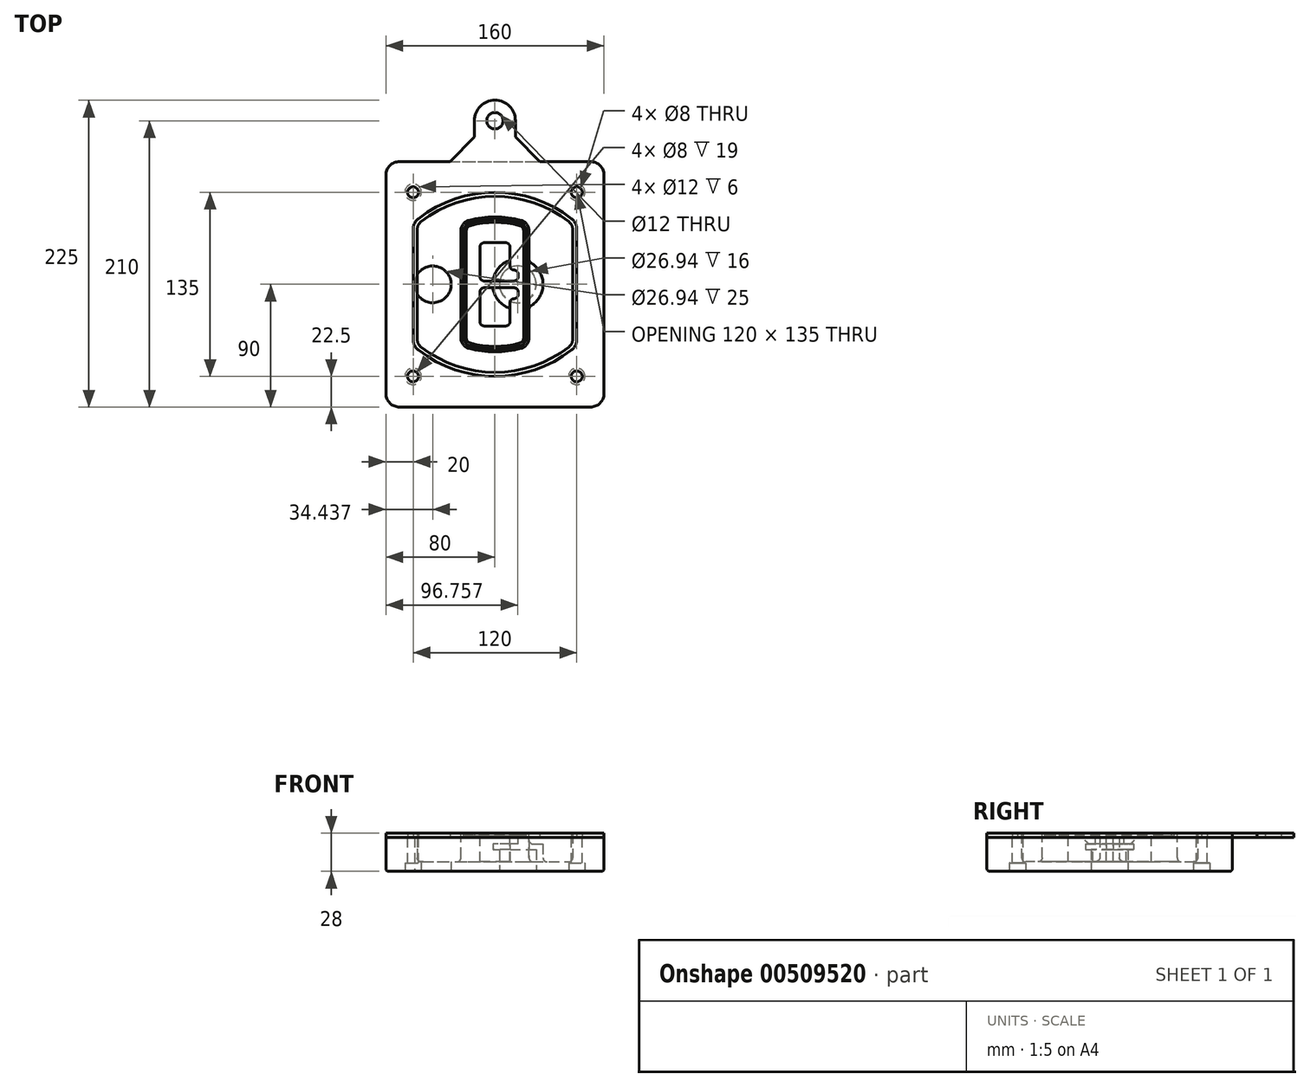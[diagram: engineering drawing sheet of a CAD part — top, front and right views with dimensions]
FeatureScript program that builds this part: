
annotation { "Feature Type Name" : "Feature", "Feature Type Description" : "" }
export const myFeature = defineFeature(function(context is Context, id is Id, definition is map)
    precondition{}
    {
        {
            var Q0;
            Q0=qCreatedBy(makeId("Top.planeOp"),FACE);
            var sketch = newSketch(context, id + "F0", { "sketchPlane" : qUnion([Q0])});
            skPoint(sketch, "E0.rect.middle", {"position": v(0, 0) * mm});
            skLineSegment(sketch, "E1.bottom", {"start": v(-70, -90) * mm, "end": v(70, -90) * mm});
            skLineSegment(sketch, "E1.top", {"start": v(-70, 90) * mm, "end": v(70, 90) * mm});
            skLineSegment(sketch, "E1.left", {"start": v(-80, -80) * mm, "end": v(-80, 80) * mm});
            skLineSegment(sketch, "E1.right", {"start": v(80, -80) * mm, "end": v(80, 80) * mm});
            skLineSegment(sketch, "E2", {"start": v(-80, 90) * mm, "end": v(80, -90) * mm, "construction": true});
            skLineSegment(sketch, "E3", {"start": v(80, 90) * mm, "end": v(-80, -90) * mm, "construction": true});
            skCircle(sketch, "E4", {"center": v(-60, 67.5) * mm, "radius": 4 * mm});
            skCircle(sketch, "E5", {"center": v(60, 67.5) * mm, "radius": 4 * mm});
            skCircle(sketch, "E6", {"center": v(60, -67.5) * mm, "radius": 4 * mm});
            skCircle(sketch, "E7", {"center": v(-60, -67.5) * mm, "radius": 4 * mm});
            skLineSegment(sketch, "E8", {"start": v(-60, 67.5) * mm, "end": v(60, 67.5) * mm, "construction": true});
            skLineSegment(sketch, "E9", {"start": v(60, 67.5) * mm, "end": v(60, -67.5) * mm, "construction": true});
            skLineSegment(sketch, "E10", {"start": v(60, -67.5) * mm, "end": v(-60, -67.5) * mm, "construction": true});
            skLineSegment(sketch, "E11", {"start": v(-60, -67.5) * mm, "end": v(-60, 67.5) * mm, "construction": true});
            skLineSegment(sketch, "E12", {"start": v(-60, 40.3) * mm, "end": v(-60, -40.3) * mm});
            skLineSegment(sketch, "E13", {"start": v(60, 40.3) * mm, "end": v(60, -40.3) * mm});
            skArc(sketch, "E14", {"start": v(56.15, 48.18) * mm, "mid": v(0, 67.5) * mm, "end": v(-56.15, 48.18) * mm});
            skArc(sketch, "E15", {"start": v(-56.15, -48.18) * mm, "mid": v(0, -67.5) * mm, "end": v(56.15, -48.18) * mm});
            skLineSegment(sketch, "E16", {"start": v(-60, 0) * mm, "end": v(60, 0) * mm, "construction": true});
            skPoint(sketch, "E17.visualSharp", {"position": v(-60, -45) * mm});
            skArc(sketch, "E17.filletArc", {"start": v(-60, -40.3) * mm, "mid": v(-58.99, -44.68) * mm, "end": v(-56.15, -48.18) * mm});
            skPoint(sketch, "E18.visualSharp", {"position": v(-60, 45) * mm});
            skArc(sketch, "E18.filletArc", {"start": v(-56.15, 48.18) * mm, "mid": v(-58.99, 44.68) * mm, "end": v(-60, 40.3) * mm});
            skPoint(sketch, "E19.visualSharp", {"position": v(60, 45) * mm});
            skArc(sketch, "E19.filletArc", {"start": v(60, 40.3) * mm, "mid": v(58.99, 44.68) * mm, "end": v(56.15, 48.18) * mm});
            skPoint(sketch, "E20.visualSharp", {"position": v(60, -45) * mm});
            skArc(sketch, "E20.filletArc", {"start": v(56.15, -48.18) * mm, "mid": v(58.99, -44.68) * mm, "end": v(60, -40.3) * mm});
            skPoint(sketch, "E21.visualSharp", {"position": v(-80, 90) * mm});
            skArc(sketch, "E21.filletArc", {"start": v(-70, 90) * mm, "mid": v(-77.07, 87.07) * mm, "end": v(-80, 80) * mm});
            skPoint(sketch, "E22.visualSharp", {"position": v(80, 90) * mm});
            skArc(sketch, "E22.filletArc", {"start": v(80, 80) * mm, "mid": v(77.07, 87.07) * mm, "end": v(70, 90) * mm});
            skPoint(sketch, "E23.visualSharp", {"position": v(80, -90) * mm});
            skArc(sketch, "E23.filletArc", {"start": v(70, -90) * mm, "mid": v(77.07, -87.07) * mm, "end": v(80, -80) * mm});
            skPoint(sketch, "E24.visualSharp", {"position": v(-80, -90) * mm});
            skArc(sketch, "E24.filletArc", {"start": v(-80, -80) * mm, "mid": v(-77.07, -87.07) * mm, "end": v(-70, -90) * mm});
            skArc(sketch, "E25.0", {"start": v(57, 40.3) * mm, "mid": v(56.3, 43.36) * mm, "end": v(54.3, 45.81) * mm});
            skLineSegment(sketch, "E25.1", {"start": v(57, 40.3) * mm, "end": v(57, -40.3) * mm});
            skArc(sketch, "E25.2", {"start": v(54.3, -45.81) * mm, "mid": v(56.3, -43.36) * mm, "end": v(57, -40.3) * mm});
            skArc(sketch, "E25.3", {"start": v(-54.3, -45.81) * mm, "mid": v(0, -64.5) * mm, "end": v(54.3, -45.81) * mm});
            skArc(sketch, "E25.4", {"start": v(-57, -40.3) * mm, "mid": v(-56.3, -43.36) * mm, "end": v(-54.3, -45.81) * mm});
            skArc(sketch, "E25.5", {"start": v(54.3, 45.81) * mm, "mid": v(0, 64.5) * mm, "end": v(-54.3, 45.81) * mm});
            skLineSegment(sketch, "E25.6", {"start": v(-57, 40.3) * mm, "end": v(-57, -40.3) * mm});
            skArc(sketch, "E25.7", {"start": v(-54.3, 45.81) * mm, "mid": v(-56.3, 43.36) * mm, "end": v(-57, 40.3) * mm});
            skArc(sketch, "E26.0", {"start": v(-58.62, 51.33) * mm, "mid": v(-62.58, 46.43) * mm, "end": v(-64, 40.3) * mm});
            skArc(sketch, "E26.1", {"start": v(58.62, 51.33) * mm, "mid": v(0, 71.5) * mm, "end": v(-58.62, 51.33) * mm});
            skArc(sketch, "E26.2", {"start": v(64, 40.3) * mm, "mid": v(62.58, 46.43) * mm, "end": v(58.62, 51.33) * mm});
            skLineSegment(sketch, "E26.3", {"start": v(64, 40.3) * mm, "end": v(64, -40.3) * mm});
            skArc(sketch, "E26.4", {"start": v(58.62, -51.33) * mm, "mid": v(62.58, -46.43) * mm, "end": v(64, -40.3) * mm});
            skLineSegment(sketch, "E26.5", {"start": v(-64, 40.3) * mm, "end": v(-64, -40.3) * mm});
            skArc(sketch, "E26.6", {"start": v(-58.62, -51.33) * mm, "mid": v(0, -71.5) * mm, "end": v(58.62, -51.33) * mm});
            skArc(sketch, "E26.7", {"start": v(-64, -40.3) * mm, "mid": v(-62.58, -46.43) * mm, "end": v(-58.62, -51.33) * mm});
            skSolve(sketch);
        }
        {
            var Q0;
            Q0=makeQuery(id+"F0.imprint","IMPRINT",FACE,{"disambiguationData":[TD([[makeQuery(id+"F0.imprint","IMPRINT",EDGE,{"derivedFrom":sQuery(id+"F0.wireOp",EDGE,"E1.bottom")}),1.0]])]});
            var Q1;
            Q1=makeQuery(id+"F0.imprint","IMPRINT",FACE,{"disambiguationData":[TD([[makeQuery(id+"F0.imprint","IMPRINT",EDGE,{"derivedFrom":sQuery(id+"F0.wireOp",EDGE,"E12")}),1.0]])]});
            var Q2;
            Q2=makeQuery(id+"F0.imprint","IMPRINT",FACE,{"disambiguationData":[TD([[makeQuery(id+"F0.imprint","IMPRINT",EDGE,{"derivedFrom":sQuery(id+"F0.wireOp",EDGE,"E25.0")}),1.0]])]});
            var Q3;
            Q3=makeQuery(id+"F0.imprint","IMPRINT",FACE,{"disambiguationData":[TD([[makeQuery(id+"F0.imprint","IMPRINT",EDGE,{"derivedFrom":sQuery(id+"F0.wireOp",EDGE,"E12")}),-1.0]])]});
            extrude(context, id + "F1", {"entities" : qUnion([Q0, Q1, Q2, Q3]), "oppositeDirection" : true, "depth" : 25 * mm});
        }
        {
            var Q0;
            Q0=makeQuery(id+"F0.imprint","IMPRINT",FACE,{"disambiguationData":[TD([[makeQuery(id+"F0.imprint","IMPRINT",EDGE,{"derivedFrom":sQuery(id+"F0.wireOp",EDGE,"E12")}),1.0]])]});
            extrude(context, id + "F2", {"entities" : qUnion([Q0]), "operationType" : NewBodyOperationType.ADD, "depth" : 3 * mm});
        }
        {
            var Q0;
            Q0=makeQuery(id+"F0.imprint","IMPRINT",FACE,{"disambiguationData":[TD([[makeQuery(id+"F0.imprint","IMPRINT",EDGE,{"derivedFrom":sQuery(id+"F0.wireOp",EDGE,"E25.0")}),1.0]])]});
            extrude(context, id + "F3", {"entities" : qUnion([Q0]), "operationType" : NewBodyOperationType.REMOVE, "oppositeDirection" : true, "depth" : 18 * mm});
        }
        {
            var Q0;
            Q0=makeQuery(id+"F2.opExtrude","CAP_FACE",FACE,{"disambiguationData":[OSD([sQuery(id+"F0.wireOp",EDGE,"E12"),sQuery(id+"F0.wireOp",EDGE,"E13"),sQuery(id+"F0.wireOp",EDGE,"E14"),sQuery(id+"F0.wireOp",EDGE,"E15"),sQuery(id+"F0.wireOp",EDGE,"E17.filletArc"),sQuery(id+"F0.wireOp",EDGE,"E18.filletArc"),sQuery(id+"F0.wireOp",EDGE,"E19.filletArc"),sQuery(id+"F0.wireOp",EDGE,"E20.filletArc"),sQuery(id+"F0.wireOp",EDGE,"E25.0"),sQuery(id+"F0.wireOp",EDGE,"E25.1"),sQuery(id+"F0.wireOp",EDGE,"E25.2"),sQuery(id+"F0.wireOp",EDGE,"E25.3"),sQuery(id+"F0.wireOp",EDGE,"E25.4"),sQuery(id+"F0.wireOp",EDGE,"E25.5"),sQuery(id+"F0.wireOp",EDGE,"E25.6"),sQuery(id+"F0.wireOp",EDGE,"E25.7")])],"isStart":false});
            var sketch = newSketch(context, id + "F4", { "sketchPlane" : qUnion([Q0])});
            skArc(sketch, "E27.0", {"start": v(-19.08, -46.97) * mm, "mid": v(0, -49.5) * mm, "end": v(19.08, -46.97) * mm});
            skArc(sketch, "E28.0", {"start": v(19.08, 46.97) * mm, "mid": v(0, 49.5) * mm, "end": v(-19.08, 46.97) * mm});
            skLineSegment(sketch, "E29", {"start": v(-25, 39.25) * mm, "end": v(-25, -39.25) * mm});
            skLineSegment(sketch, "E30", {"start": v(25, 39.25) * mm, "end": v(25, -39.25) * mm});
            skLineSegment(sketch, "E31", {"start": v(-25, 45.1) * mm, "end": v(25, 45.1) * mm, "construction": true});
            skLineSegment(sketch, "E32", {"start": v(-25, -45.1) * mm, "end": v(25, -45.1) * mm, "construction": true});
            skPoint(sketch, "E33.visualSharp", {"position": v(-25, 45.1) * mm});
            skArc(sketch, "E33.filletArc", {"start": v(-19.08, 46.97) * mm, "mid": v(-23.35, 44.11) * mm, "end": v(-25, 39.25) * mm});
            skPoint(sketch, "E34.visualSharp", {"position": v(25, 45.1) * mm});
            skArc(sketch, "E34.filletArc", {"start": v(25, 39.25) * mm, "mid": v(23.35, 44.11) * mm, "end": v(19.08, 46.97) * mm});
            skPoint(sketch, "E35.visualSharp", {"position": v(25, -45.1) * mm});
            skArc(sketch, "E35.filletArc", {"start": v(19.08, -46.97) * mm, "mid": v(23.35, -44.11) * mm, "end": v(25, -39.25) * mm});
            skPoint(sketch, "E36.visualSharp", {"position": v(-25, -45.1) * mm});
            skArc(sketch, "E36.filletArc", {"start": v(-25, -39.25) * mm, "mid": v(-23.35, -44.11) * mm, "end": v(-19.08, -46.97) * mm});
            skArc(sketch, "E37.0", {"start": v(54.3, 45.81) * mm, "mid": v(0, 64.5) * mm, "end": v(-54.3, 45.81) * mm});
            skArc(sketch, "E37.1", {"start": v(-54.3, 45.81) * mm, "mid": v(-56.3, 43.36) * mm, "end": v(-57, 40.3) * mm});
            skLineSegment(sketch, "E37.2", {"start": v(-57, 40.3) * mm, "end": v(-57, -40.3) * mm});
            skArc(sketch, "E37.3", {"start": v(-57, -40.3) * mm, "mid": v(-56.3, -43.36) * mm, "end": v(-54.3, -45.81) * mm});
            skArc(sketch, "E37.4", {"start": v(-54.3, -45.81) * mm, "mid": v(0, -64.5) * mm, "end": v(54.3, -45.81) * mm});
            skArc(sketch, "E37.5", {"start": v(54.3, -45.81) * mm, "mid": v(56.3, -43.36) * mm, "end": v(57, -40.3) * mm});
            skLineSegment(sketch, "E37.6", {"start": v(57, 40.3) * mm, "end": v(57, -40.3) * mm});
            skArc(sketch, "E37.7", {"start": v(57, 40.3) * mm, "mid": v(56.3, 43.36) * mm, "end": v(54.3, 45.81) * mm});
            skLineSegment(sketch, "E38.0", {"start": v(23, 39.25) * mm, "end": v(23, -39.25) * mm});
            skArc(sketch, "E38.1", {"start": v(18.56, -45.04) * mm, "mid": v(21.76, -42.9) * mm, "end": v(23, -39.25) * mm});
            skArc(sketch, "E38.2", {"start": v(-18.56, -45.04) * mm, "mid": v(0, -47.5) * mm, "end": v(18.56, -45.04) * mm});
            skArc(sketch, "E38.3", {"start": v(-23, -39.25) * mm, "mid": v(-21.76, -42.9) * mm, "end": v(-18.56, -45.04) * mm});
            skLineSegment(sketch, "E38.4", {"start": v(-23, 39.25) * mm, "end": v(-23, -39.25) * mm});
            skArc(sketch, "E38.5", {"start": v(23, 39.25) * mm, "mid": v(21.76, 42.9) * mm, "end": v(18.56, 45.04) * mm});
            skArc(sketch, "E38.6", {"start": v(-18.56, 45.04) * mm, "mid": v(-21.76, 42.9) * mm, "end": v(-23, 39.25) * mm});
            skArc(sketch, "E38.7", {"start": v(18.56, 45.04) * mm, "mid": v(0, 47.5) * mm, "end": v(-18.56, 45.04) * mm});
            skArc(sketch, "E39.0", {"start": v(21, 39.25) * mm, "mid": v(20.18, 41.68) * mm, "end": v(18.04, 43.1) * mm});
            skLineSegment(sketch, "E39.1", {"start": v(21, 39.25) * mm, "end": v(21, -39.25) * mm});
            skArc(sketch, "E39.2", {"start": v(18.04, -43.1) * mm, "mid": v(20.18, -41.68) * mm, "end": v(21, -39.25) * mm});
            skArc(sketch, "E39.3", {"start": v(-18.04, -43.1) * mm, "mid": v(0, -45.5) * mm, "end": v(18.04, -43.1) * mm});
            skArc(sketch, "E39.4", {"start": v(-21, -39.25) * mm, "mid": v(-20.18, -41.68) * mm, "end": v(-18.04, -43.1) * mm});
            skArc(sketch, "E39.5", {"start": v(18.04, 43.1) * mm, "mid": v(0, 45.5) * mm, "end": v(-18.04, 43.1) * mm});
            skLineSegment(sketch, "E39.6", {"start": v(-21, 39.25) * mm, "end": v(-21, -39.25) * mm});
            skArc(sketch, "E39.7", {"start": v(-18.04, 43.1) * mm, "mid": v(-20.18, 41.68) * mm, "end": v(-21, 39.25) * mm});
            skLineSegment(sketch, "E40", {"start": v(-25, 0) * mm, "end": v(25, 0) * mm, "construction": true});
            skLineSegment(sketch, "E41", {"start": v(-11, 5.5) * mm, "end": v(-11, 27.5) * mm});
            skLineSegment(sketch, "E42", {"start": v(-8, 30.5) * mm, "end": v(8, 30.5) * mm});
            skLineSegment(sketch, "E43", {"start": v(11, 27.5) * mm, "end": v(11, 13.5) * mm});
            skLineSegment(sketch, "E44", {"start": v(14, 10.5) * mm, "end": v(14, 10.5) * mm});
            skLineSegment(sketch, "E45", {"start": v(17, 7.5) * mm, "end": v(17, 5.5) * mm});
            skLineSegment(sketch, "E46", {"start": v(14, 2.5) * mm, "end": v(-8, 2.5) * mm});
            skPoint(sketch, "E47.visualSharp", {"position": v(-11, 30.5) * mm});
            skArc(sketch, "E47.filletArc", {"start": v(-8, 30.5) * mm, "mid": v(-10.12, 29.62) * mm, "end": v(-11, 27.5) * mm});
            skPoint(sketch, "E48.visualSharp", {"position": v(11, 30.5) * mm});
            skArc(sketch, "E48.filletArc", {"start": v(11, 27.5) * mm, "mid": v(10.12, 29.62) * mm, "end": v(8, 30.5) * mm});
            skPoint(sketch, "E49.visualSharp", {"position": v(11, 10.5) * mm});
            skArc(sketch, "E49.filletArc", {"start": v(11, 13.5) * mm, "mid": v(11.88, 11.38) * mm, "end": v(14, 10.5) * mm});
            skPoint(sketch, "E50.visualSharp", {"position": v(17, 10.5) * mm});
            skArc(sketch, "E50.filletArc", {"start": v(17, 7.5) * mm, "mid": v(16.12, 9.62) * mm, "end": v(14, 10.5) * mm});
            skPoint(sketch, "E51.visualSharp", {"position": v(17, 2.5) * mm});
            skArc(sketch, "E51.filletArc", {"start": v(14, 2.5) * mm, "mid": v(16.12, 3.38) * mm, "end": v(17, 5.5) * mm});
            skPoint(sketch, "E52.visualSharp", {"position": v(-11, 2.5) * mm});
            skArc(sketch, "E52.filletArc", {"start": v(-11, 5.5) * mm, "mid": v(-10.12, 3.38) * mm, "end": v(-8, 2.5) * mm});
            skLineSegment(sketch, "E53.0.MirrorCS", {"start": v(14, -2.5) * mm, "end": v(-8, -2.5) * mm});
            skArc(sketch, "E54.0.MirrorCS", {"start": v(-11, -5.5) * mm, "mid": v(-10.12, -3.38) * mm, "end": v(-8, -2.5) * mm});
            skLineSegment(sketch, "E55.0.MirrorCS", {"start": v(-11, -5.5) * mm, "end": v(-11, -27.5) * mm});
            skArc(sketch, "E56.0.MirrorCS", {"start": v(-8, -30.5) * mm, "mid": v(-10.12, -29.62) * mm, "end": v(-11, -27.5) * mm});
            skLineSegment(sketch, "E57.0.MirrorCS", {"start": v(-8, -30.5) * mm, "end": v(8, -30.5) * mm});
            skArc(sketch, "E58.0.MirrorCS", {"start": v(11, -27.5) * mm, "mid": v(10.12, -29.62) * mm, "end": v(8, -30.5) * mm});
            skLineSegment(sketch, "E59.0.MirrorCS", {"start": v(11, -27.5) * mm, "end": v(11, -13.5) * mm});
            skArc(sketch, "E60.0.MirrorCS", {"start": v(11, -13.5) * mm, "mid": v(11.88, -11.38) * mm, "end": v(14, -10.5) * mm});
            skArc(sketch, "E61.0.MirrorCS", {"start": v(17, -7.5) * mm, "mid": v(16.12, -9.62) * mm, "end": v(14, -10.5) * mm});
            skLineSegment(sketch, "E62.0.MirrorCS", {"start": v(17, -7.5) * mm, "end": v(17, -5.5) * mm});
            skArc(sketch, "E63.0.MirrorCS", {"start": v(14, -2.5) * mm, "mid": v(16.12, -3.38) * mm, "end": v(17, -5.5) * mm});
            skSolve(sketch);
        }
        {
            var Q0;
            Q0=makeQuery(id+"F4.imprint","IMPRINT",FACE,{"disambiguationData":[TD([[makeQuery(id+"F4.imprint","IMPRINT",EDGE,{"derivedFrom":sQuery(id+"F4.wireOp",EDGE,"E27.0")}),1.0]])]});
            var Q1;
            Q1=makeQuery(id+"F4.imprint","IMPRINT",FACE,{"disambiguationData":[TD([[makeQuery(id+"F4.imprint","IMPRINT",EDGE,{"derivedFrom":sQuery(id+"F4.wireOp",EDGE,"E38.0")}),-1.0]])]});
            var Q2;
            Q2=makeQuery(id+"F4.imprint","IMPRINT",FACE,{"disambiguationData":[TD([[makeQuery(id+"F4.imprint","IMPRINT",EDGE,{"derivedFrom":sQuery(id+"F4.wireOp",EDGE,"E39.0")}),1.0]])]});
            extrude(context, id + "F5", {"entities" : qUnion([Q0, Q1, Q2]), "operationType" : NewBodyOperationType.ADD, "endBound" : BoundingType.UP_TO_NEXT, "oppositeDirection" : true, "depth" : 25 * mm});
        }
        {
            var Q0;
            Q0=makeQuery(id+"F4.imprint","IMPRINT",FACE,{"disambiguationData":[TD([[makeQuery(id+"F4.imprint","IMPRINT",EDGE,{"derivedFrom":sQuery(id+"F4.wireOp",EDGE,"E38.0")}),-1.0]])]});
            extrude(context, id + "F6", {"entities" : qUnion([Q0]), "operationType" : NewBodyOperationType.REMOVE, "oppositeDirection" : true, "depth" : 2 * mm});
        }
        {
            var Q0;
            Q0=makeQuery(id+"F1.opExtrude","CAP_FACE",FACE,{"disambiguationData":[OSD([sQuery(id+"F0.wireOp",EDGE,"E1.bottom"),sQuery(id+"F0.wireOp",EDGE,"E1.top"),sQuery(id+"F0.wireOp",EDGE,"E1.left"),sQuery(id+"F0.wireOp",EDGE,"E1.right"),sQuery(id+"F0.wireOp",EDGE,"E4"),sQuery(id+"F0.wireOp",EDGE,"E5"),sQuery(id+"F0.wireOp",EDGE,"E6"),sQuery(id+"F0.wireOp",EDGE,"E7"),sQuery(id+"F0.wireOp",EDGE,"E21.filletArc"),sQuery(id+"F0.wireOp",EDGE,"E22.filletArc"),sQuery(id+"F0.wireOp",EDGE,"E23.filletArc"),sQuery(id+"F0.wireOp",EDGE,"E24.filletArc")])],"isStart":false});
            var sketch = newSketch(context, id + "F7", { "sketchPlane" : qUnion([Q0])});
            skCircle(sketch, "E64", {"center": v(16.76, 0) * mm, "radius": 13.47 * mm});
            skCircle(sketch, "E65", {"center": v(-45.56, 0) * mm, "radius": 13.47 * mm});
            skLineSegment(sketch, "E66", {"start": v(80, 0) * mm, "end": v(-80, 0) * mm});
            skCircle(sketch, "E67", {"center": v(16.76, 0) * mm, "radius": 18.47 * mm});
            skCircle(sketch, "E68", {"center": v(60, -67.5) * mm, "radius": 6 * mm});
            skCircle(sketch, "E69", {"center": v(-60, -67.5) * mm, "radius": 6 * mm});
            skCircle(sketch, "E70", {"center": v(-60, 67.5) * mm, "radius": 6 * mm});
            skCircle(sketch, "E71", {"center": v(60, 67.5) * mm, "radius": 6 * mm});
            skSolve(sketch);
        }
        {
            var Q0;
            {var subQ1=sQuery(id+"F7.wireOp",EDGE,"E66");var subQ4=sQuery(id+"F7.wireOp",EDGE,"E64");var subQ6=makeQuery(id+"F7.imprint","INTERSECT",VERTEX,{"disambiguationData":[OD(0.0)],"derivedFrom":[subQ4,subQ1]});Q0=makeQuery(id+"F7.imprint","IMPRINT",FACE,{"disambiguationData":[TD([[makeQuery(id+"F7.imprint","IMPRINT",EDGE,{"disambiguationData":[TD([[subQ6,-1.0]])],"derivedFrom":subQ4}),-1.0]])]});}
            var Q1;
            {var subQ0=sQuery(id+"F7.wireOp",EDGE,"E66");var subQ1=sQuery(id+"F7.wireOp",EDGE,"E64");var subQ3=makeQuery(id+"F7.imprint","INTERSECT",VERTEX,{"disambiguationData":[OD(0.0)],"derivedFrom":[subQ1,subQ0]});Q1=makeQuery(id+"F7.imprint","IMPRINT",FACE,{"disambiguationData":[TD([[makeQuery(id+"F7.imprint","IMPRINT",EDGE,{"disambiguationData":[TD([[subQ3,-1.0]])],"derivedFrom":subQ1}),1.0]])]});}
            var Q2;
            {var subQ0=sQuery(id+"F7.wireOp",EDGE,"E66");var subQ1=sQuery(id+"F7.wireOp",EDGE,"E64");var subQ3=makeQuery(id+"F7.imprint","INTERSECT",VERTEX,{"disambiguationData":[OD(0.0)],"derivedFrom":[subQ1,subQ0]});Q2=makeQuery(id+"F7.imprint","IMPRINT",FACE,{"disambiguationData":[TD([[makeQuery(id+"F7.imprint","IMPRINT",EDGE,{"disambiguationData":[TD([[subQ3,1.0]])],"derivedFrom":subQ1}),1.0]])]});}
            var Q3;
            {var subQ1=sQuery(id+"F7.wireOp",EDGE,"E66");var subQ4=sQuery(id+"F7.wireOp",EDGE,"E64");var subQ6=makeQuery(id+"F7.imprint","INTERSECT",VERTEX,{"disambiguationData":[OD(0.0)],"derivedFrom":[subQ4,subQ1]});Q3=makeQuery(id+"F7.imprint","IMPRINT",FACE,{"disambiguationData":[TD([[makeQuery(id+"F7.imprint","IMPRINT",EDGE,{"disambiguationData":[TD([[subQ6,1.0]])],"derivedFrom":subQ4}),-1.0]])]});}
            extrude(context, id + "F8", {"entities" : qUnion([Q0, Q1, Q2, Q3]), "operationType" : NewBodyOperationType.ADD, "oppositeDirection" : true, "depth" : 20 * mm});
        }
        {
            var Q0;
            {var subQ0=sQuery(id+"F7.wireOp",EDGE,"E66");var subQ1=sQuery(id+"F7.wireOp",EDGE,"E64");var subQ3=makeQuery(id+"F7.imprint","INTERSECT",VERTEX,{"disambiguationData":[OD(0.0)],"derivedFrom":[subQ1,subQ0]});Q0=makeQuery(id+"F7.imprint","IMPRINT",FACE,{"disambiguationData":[TD([[makeQuery(id+"F7.imprint","IMPRINT",EDGE,{"disambiguationData":[TD([[subQ3,-1.0]])],"derivedFrom":subQ1}),1.0]])]});}
            var Q1;
            {var subQ0=sQuery(id+"F7.wireOp",EDGE,"E66");var subQ1=sQuery(id+"F7.wireOp",EDGE,"E64");var subQ3=makeQuery(id+"F7.imprint","INTERSECT",VERTEX,{"disambiguationData":[OD(0.0)],"derivedFrom":[subQ1,subQ0]});Q1=makeQuery(id+"F7.imprint","IMPRINT",FACE,{"disambiguationData":[TD([[makeQuery(id+"F7.imprint","IMPRINT",EDGE,{"disambiguationData":[TD([[subQ3,1.0]])],"derivedFrom":subQ1}),1.0]])]});}
            extrude(context, id + "F9", {"entities" : qUnion([Q0, Q1]), "operationType" : NewBodyOperationType.REMOVE, "oppositeDirection" : true, "depth" : 16 * mm});
        }
        {
            var Q0;
            {var subQ0=sQuery(id+"F7.wireOp",EDGE,"E66");var subQ1=sQuery(id+"F7.wireOp",EDGE,"E65");var subQ3=makeQuery(id+"F7.imprint","INTERSECT",VERTEX,{"disambiguationData":[OD(0.0)],"derivedFrom":[subQ1,subQ0]});Q0=makeQuery(id+"F7.imprint","IMPRINT",FACE,{"disambiguationData":[TD([[makeQuery(id+"F7.imprint","IMPRINT",EDGE,{"disambiguationData":[TD([[subQ3,-1.0]])],"derivedFrom":subQ1}),1.0]])]});}
            var Q1;
            {var subQ0=sQuery(id+"F7.wireOp",EDGE,"E66");var subQ1=sQuery(id+"F7.wireOp",EDGE,"E65");var subQ3=makeQuery(id+"F7.imprint","INTERSECT",VERTEX,{"disambiguationData":[OD(0.0)],"derivedFrom":[subQ1,subQ0]});Q1=makeQuery(id+"F7.imprint","IMPRINT",FACE,{"disambiguationData":[TD([[makeQuery(id+"F7.imprint","IMPRINT",EDGE,{"disambiguationData":[TD([[subQ3,1.0]])],"derivedFrom":subQ1}),1.0]])]});}
            extrude(context, id + "F10", {"entities" : qUnion([Q0, Q1]), "operationType" : NewBodyOperationType.REMOVE, "oppositeDirection" : true, "depth" : 25 * mm});
        }
        {
            var Q0;
            Q0=makeQuery(id+"F7.imprint","IMPRINT",FACE,{"disambiguationData":[TD([[makeQuery(id+"F7.imprint","IMPRINT",EDGE,{"derivedFrom":sQuery(id+"F7.wireOp",EDGE,"E68")}),1.0]])]});
            var Q1;
            Q1=makeQuery(id+"F7.imprint","IMPRINT",FACE,{"disambiguationData":[TD([[makeQuery(id+"F7.imprint","IMPRINT",EDGE,{"derivedFrom":makeQuery(id+"F1.opExtrude","CAP_EDGE",EDGE,{"disambiguationData":[OSD([sQuery(id+"F0.wireOp",EDGE,"E5")])],"isStart":false})}),-1.0]])]});
            var Q2;
            Q2=makeQuery(id+"F7.imprint","IMPRINT",FACE,{"disambiguationData":[TD([[makeQuery(id+"F7.imprint","IMPRINT",EDGE,{"derivedFrom":sQuery(id+"F7.wireOp",EDGE,"E69")}),1.0]])]});
            var Q3;
            Q3=makeQuery(id+"F7.imprint","IMPRINT",FACE,{"disambiguationData":[TD([[makeQuery(id+"F7.imprint","IMPRINT",EDGE,{"derivedFrom":makeQuery(id+"F1.opExtrude","CAP_EDGE",EDGE,{"disambiguationData":[OSD([sQuery(id+"F0.wireOp",EDGE,"E4")])],"isStart":false})}),-1.0]])]});
            var Q4;
            Q4=makeQuery(id+"F7.imprint","IMPRINT",FACE,{"disambiguationData":[TD([[makeQuery(id+"F7.imprint","IMPRINT",EDGE,{"derivedFrom":sQuery(id+"F7.wireOp",EDGE,"E70")}),1.0]])]});
            var Q5;
            Q5=makeQuery(id+"F7.imprint","IMPRINT",FACE,{"disambiguationData":[TD([[makeQuery(id+"F7.imprint","IMPRINT",EDGE,{"derivedFrom":makeQuery(id+"F1.opExtrude","CAP_EDGE",EDGE,{"disambiguationData":[OSD([sQuery(id+"F0.wireOp",EDGE,"E7")])],"isStart":false})}),-1.0]])]});
            var Q6;
            Q6=makeQuery(id+"F7.imprint","IMPRINT",FACE,{"disambiguationData":[TD([[makeQuery(id+"F7.imprint","IMPRINT",EDGE,{"derivedFrom":sQuery(id+"F7.wireOp",EDGE,"E71")}),1.0]])]});
            var Q7;
            Q7=makeQuery(id+"F7.imprint","IMPRINT",FACE,{"disambiguationData":[TD([[makeQuery(id+"F7.imprint","IMPRINT",EDGE,{"derivedFrom":makeQuery(id+"F1.opExtrude","CAP_EDGE",EDGE,{"disambiguationData":[OSD([sQuery(id+"F0.wireOp",EDGE,"E6")])],"isStart":false})}),-1.0]])]});
            extrude(context, id + "F11", {"entities" : qUnion([Q0, Q1, Q2, Q3, Q4, Q5, Q6, Q7]), "operationType" : NewBodyOperationType.REMOVE, "oppositeDirection" : true, "depth" : 6 * mm});
        }
        {
            var Q0;
            Q0=makeQuery(id+"F9.boolean.opBoolean","COPY",FACE,{"derivedFrom":makeQuery(id+"F9.opExtrude","CAP_FACE",FACE,{"disambiguationData":[OSD([sQuery(id+"F7.wireOp",EDGE,"E64")])],"isStart":false})});
            var sketch = newSketch(context, id + "F12", { "sketchPlane" : qUnion([Q0])});
            skArc(sketch, "E72.0", {"start": v(11, 17.55) * mm, "mid": v(2.57, 11.82) * mm, "end": v(-1.54, 2.5) * mm});
            skArc(sketch, "E72.1", {"start": v(-1.54, -2.5) * mm, "mid": v(2.57, -11.82) * mm, "end": v(11, -17.55) * mm});
            skLineSegment(sketch, "E73", {"start": v(-1.54, -2.5) * mm, "end": v(14, -2.5) * mm});
            skLineSegment(sketch, "E74.0", {"start": v(14, 2.5) * mm, "end": v(-1.54, 2.5) * mm});
            skArc(sketch, "E74.1", {"start": v(14, 2.5) * mm, "mid": v(16.12, 3.38) * mm, "end": v(17, 5.5) * mm});
            skLineSegment(sketch, "E74.2", {"start": v(17, 7.5) * mm, "end": v(17, 5.5) * mm});
            skArc(sketch, "E74.3", {"start": v(17, 7.5) * mm, "mid": v(16.12, 9.62) * mm, "end": v(14, 10.5) * mm});
            skArc(sketch, "E74.4", {"start": v(11, 13.5) * mm, "mid": v(11.88, 11.38) * mm, "end": v(14, 10.5) * mm});
            skLineSegment(sketch, "E74.5", {"start": v(11, 17.55) * mm, "end": v(11, 13.5) * mm});
            skLineSegment(sketch, "E74.7", {"start": v(14, -2.5) * mm, "end": v(-1.54, -2.5) * mm});
            skArc(sketch, "E74.8", {"start": v(14, -2.5) * mm, "mid": v(16.12, -3.38) * mm, "end": v(17, -5.5) * mm});
            skLineSegment(sketch, "E74.9", {"start": v(17, -7.5) * mm, "end": v(17, -5.5) * mm});
            skArc(sketch, "E74.10", {"start": v(17, -7.5) * mm, "mid": v(16.12, -9.62) * mm, "end": v(14, -10.5) * mm});
            skArc(sketch, "E74.11", {"start": v(11, -13.5) * mm, "mid": v(11.88, -11.38) * mm, "end": v(14, -10.5) * mm});
            skLineSegment(sketch, "E74.12", {"start": v(11, -17.55) * mm, "end": v(11, -13.5) * mm});
            skPoint(sketch, "E75.orphan", {"position": v(11, -27.5) * mm});
            skPoint(sketch, "E76.orphan", {"position": v(-8, -2.5) * mm});
            skPoint(sketch, "E77.orphan", {"position": v(-8, 2.5) * mm});
            skPoint(sketch, "E78.orphan", {"position": v(11, 27.5) * mm});
            skSolve(sketch);
        }
        {
            var Q0;
            {var subQ7=sQuery(id+"F12.wireOp",EDGE,"E72.0");var subQ14=sQuery(id+"F12.wireOp",EDGE,"E72.1");var subQ16=sQuery(id+"F12.wireOp",EDGE,"E74.1");var subQ18=sQuery(id+"F12.wireOp",EDGE,"E74.8");Q0=qUnion([makeQuery(id+"F12.imprint","IMPRINT",FACE,{"disambiguationData":[TD([[makeQuery(id+"F12.imprint","IMPRINT",EDGE,{"derivedFrom":subQ7}),1.0]])]}),makeQuery(id+"F12.imprint","IMPRINT",FACE,{"disambiguationData":[TD([[makeQuery(id+"F12.imprint","IMPRINT",EDGE,{"derivedFrom":subQ14}),1.0]])]}),makeQuery(id+"F12.imprint","IMPRINT",FACE,{"disambiguationData":[TD([[makeQuery(id+"F12.imprint","IMPRINT",EDGE,{"derivedFrom":subQ16}),1.0]])]}),makeQuery(id+"F12.imprint","IMPRINT",FACE,{"disambiguationData":[TD([[makeQuery(id+"F12.imprint","IMPRINT",EDGE,{"derivedFrom":subQ18}),-1.0]])]})]);}
            var Q1;
            Q1=makeQuery(id+"F5.boolean.opBoolean","SPLIT",FACE,{"disambiguationData":[TD([makeQuery(id+"F5.opExtrude","SWEPT_FACE",FACE,{"disambiguationData":[OSD([sQuery(id+"F4.wireOp",EDGE,"E41")])]})])],"derivedFrom":makeQuery(id+"F3.boolean.opBoolean","COPY",FACE,{"derivedFrom":makeQuery(id+"F3.opExtrude","CAP_FACE",FACE,{"disambiguationData":[OSD([sQuery(id+"F0.wireOp",EDGE,"E25.0"),sQuery(id+"F0.wireOp",EDGE,"E25.1"),sQuery(id+"F0.wireOp",EDGE,"E25.2"),sQuery(id+"F0.wireOp",EDGE,"E25.3"),sQuery(id+"F0.wireOp",EDGE,"E25.4"),sQuery(id+"F0.wireOp",EDGE,"E25.5"),sQuery(id+"F0.wireOp",EDGE,"E25.6"),sQuery(id+"F0.wireOp",EDGE,"E25.7")])],"isStart":false})})});
            extrude(context, id + "F13", {"entities" : qUnion([Q0]), "operationType" : NewBodyOperationType.REMOVE, "endBound" : BoundingType.UP_TO_SURFACE, "endBoundEntityFace" : qUnion([Q1]), "depth" : 25 * mm});
        }
        {
            var Q0;
            Q0=makeQuery(id+"F3.boolean.opBoolean","COPY",EDGE,{"derivedFrom":makeQuery(id+"F3.opExtrude","CAP_EDGE",EDGE,{"disambiguationData":[OSD([sQuery(id+"F0.wireOp",EDGE,"E25.6")])],"isStart":false})});
            var Q1;
            Q1=makeQuery(id+"F8.boolean.opBoolean","INTERSECT",EDGE,{"derivedFrom":[makeQuery(id+"F5.opExtrude","SWEPT_FACE",FACE,{"disambiguationData":[OSD([sQuery(id+"F4.wireOp",EDGE,"E30")])]}),makeQuery(id+"F8.opExtrude","CAP_FACE",FACE,{"disambiguationData":[OSD([sQuery(id+"F7.wireOp",EDGE,"E67")])],"isStart":false})]});
            var Q2;
            Q2=makeQuery(id+"F8.boolean.opBoolean","INTERSECT",EDGE,{"disambiguationData":[OD(1.0)],"derivedFrom":[makeQuery(id+"F5.opExtrude","SWEPT_FACE",FACE,{"disambiguationData":[OSD([sQuery(id+"F4.wireOp",EDGE,"E30")])]}),makeQuery(id+"F8.opExtrude","SWEPT_FACE",FACE,{"disambiguationData":[OSD([sQuery(id+"F7.wireOp",EDGE,"E67")])]})]});
            var Q3;
            {var subQ0=sQuery(id+"F4.wireOp",EDGE,"E30");Q3=makeQuery(id+"F8.boolean.opBoolean","SPLIT",EDGE,{"disambiguationData":[TD([makeQuery(id+"F5.opExtrude","SWEPT_FACE",FACE,{"disambiguationData":[OSD([sQuery(id+"F4.wireOp",EDGE,"E35.filletArc")])]})])],"derivedFrom":makeQuery(id+"F5.opExtrude","CAP_EDGE",EDGE,{"disambiguationData":[OSD([subQ0])],"isStart":false})});}
            var Q4;
            {var subQ0=sQuery(id+"F0.wireOp",EDGE,"E25.7");var subQ1=sQuery(id+"F0.wireOp",EDGE,"E25.1");var subQ2=sQuery(id+"F0.wireOp",EDGE,"E25.6");var subQ3=sQuery(id+"F0.wireOp",EDGE,"E25.5");var subQ4=sQuery(id+"F0.wireOp",EDGE,"E25.4");var subQ5=sQuery(id+"F0.wireOp",EDGE,"E25.0");var subQ6=sQuery(id+"F0.wireOp",EDGE,"E25.2");var subQ7=sQuery(id+"F0.wireOp",EDGE,"E25.3");Q4=makeQuery(id+"F8.boolean.opBoolean","INTERSECT",EDGE,{"derivedFrom":[makeQuery(id+"F5.boolean.opBoolean","SPLIT",FACE,{"disambiguationData":[TD([makeQuery(id+"F2.opExtrude","SWEPT_FACE",FACE,{"disambiguationData":[OSD([subQ5])]})])],"derivedFrom":makeQuery(id+"F3.boolean.opBoolean","COPY",FACE,{"derivedFrom":makeQuery(id+"F3.opExtrude","CAP_FACE",FACE,{"disambiguationData":[OSD([subQ5,subQ1,subQ6,subQ7,subQ4,subQ3,subQ2,subQ0])],"isStart":false})})}),makeQuery(id+"F8.opExtrude","SWEPT_FACE",FACE,{"disambiguationData":[OSD([sQuery(id+"F7.wireOp",EDGE,"E67")])]})]});}
            var Q5;
            Q5=makeQuery(id+"F8.boolean.opBoolean","INTERSECT",EDGE,{"disambiguationData":[OD(0.0)],"derivedFrom":[makeQuery(id+"F5.opExtrude","SWEPT_FACE",FACE,{"disambiguationData":[OSD([sQuery(id+"F4.wireOp",EDGE,"E30")])]}),makeQuery(id+"F8.opExtrude","SWEPT_FACE",FACE,{"disambiguationData":[OSD([sQuery(id+"F7.wireOp",EDGE,"E67")])]})]});
            fillet(context, id + "F14", {"entities" : qUnion([Q0, Q1, Q2, Q3, Q4, Q5]), "radius" : 3 * mm, "tangentPropagation" : true, "allowEdgeOverflow" : false});
        }
        {
            var Q0;
            Q0=makeQuery(id+"F1.opExtrude","CAP_EDGE",EDGE,{"disambiguationData":[OSD([sQuery(id+"F0.wireOp",EDGE,"E1.bottom")])],"isStart":false});
            fillet(context, id + "F15", {"entities" : qUnion([Q0]), "radius" : 2 * mm, "tangentPropagation" : true, "allowEdgeOverflow" : false});
        }
        {
            var Q0;
            {var subQ0=sQuery(id+"F0.wireOp",EDGE,"E21.filletArc");var subQ1=sQuery(id+"F0.wireOp",EDGE,"E7");var subQ2=sQuery(id+"F0.wireOp",EDGE,"E6");var subQ3=sQuery(id+"F0.wireOp",EDGE,"E5");var subQ4=sQuery(id+"F0.wireOp",EDGE,"E4");var subQ5=sQuery(id+"F0.wireOp",EDGE,"E22.filletArc");var subQ6=sQuery(id+"F0.wireOp",EDGE,"E1.bottom");var subQ7=sQuery(id+"F0.wireOp",EDGE,"E1.right");var subQ8=sQuery(id+"F0.wireOp",EDGE,"E1.top");var subQ9=sQuery(id+"F0.wireOp",EDGE,"E1.left");var subQ10=sQuery(id+"F0.wireOp",EDGE,"E23.filletArc");var subQ11=sQuery(id+"F0.wireOp",EDGE,"E24.filletArc");Q0=makeQuery(id+"F2.boolean.opBoolean","SPLIT",FACE,{"disambiguationData":[TD([makeQuery(id+"F1.opExtrude","SWEPT_FACE",FACE,{"disambiguationData":[OSD([subQ6])]})])],"derivedFrom":makeQuery(id+"F1.opExtrude","CAP_FACE",FACE,{"disambiguationData":[OSD([subQ6,subQ8,subQ9,subQ7,subQ4,subQ3,subQ2,subQ1,subQ0,subQ5,subQ10,subQ11])],"isStart":true})});}
            var sketch = newSketch(context, id + "F16", { "sketchPlane" : qUnion([Q0])});
            skLineSegment(sketch, "E79", {"start": v(0, 90) * mm, "end": v(0, 120) * mm, "construction": true});
            skCircle(sketch, "E80", {"center": v(0, 120) * mm, "radius": 6 * mm});
            skLineSegment(sketch, "E81", {"start": v(-33, 90) * mm, "end": v(-15, 108) * mm});
            skLineSegment(sketch, "E82", {"start": v(-15, 108) * mm, "end": v(-15, 120) * mm});
            skLineSegment(sketch, "E83", {"start": v(15, 120) * mm, "end": v(15, 108) * mm});
            skLineSegment(sketch, "E84", {"start": v(15, 108) * mm, "end": v(33, 90) * mm});
            skArc(sketch, "E85", {"start": v(15, 120) * mm, "mid": v(0, 135) * mm, "end": v(-15, 120) * mm});
            skLineSegment(sketch, "E86", {"start": v(-80, 0) * mm, "end": v(80, 0) * mm, "construction": true});
            skArc(sketch, "E87.MirrorCS", {"start": v(15, -120) * mm, "mid": v(0, -135) * mm, "end": v(-15, -120) * mm});
            skLineSegment(sketch, "E88.MirrorCS", {"start": v(15, -108) * mm, "end": v(33, -90) * mm});
            skLineSegment(sketch, "E89.MirrorCS", {"start": v(-15, -108) * mm, "end": v(-15, -120) * mm});
            skLineSegment(sketch, "E90.MirrorCS", {"start": v(0, -90) * mm, "end": v(0, -120) * mm, "construction": true});
            skLineSegment(sketch, "E91.MirrorCS", {"start": v(15, -120) * mm, "end": v(15, -108) * mm});
            skCircle(sketch, "E92.MirrorC", {"center": v(0, -120) * mm, "radius": 6 * mm});
            skLineSegment(sketch, "E93.MirrorCS", {"start": v(-33, -90) * mm, "end": v(-15, -108) * mm});
            skSolve(sketch);
        }
        {
            var Q0;
            Q0=makeQuery(id+"F16.imprint","IMPRINT",FACE,{"disambiguationData":[TD([[makeQuery(id+"F16.imprint","IMPRINT",EDGE,{"derivedFrom":makeQuery(id+"F1.opExtrude","CAP_EDGE",EDGE,{"disambiguationData":[OSD([sQuery(id+"F0.wireOp",EDGE,"E1.left")])],"isStart":true})}),-1.0]])]});
            var Q1;
            Q1=makeQuery(id+"F16.imprint","IMPRINT",FACE,{"disambiguationData":[TD([[makeQuery(id+"F16.imprint","IMPRINT",EDGE,{"derivedFrom":sQuery(id+"F16.wireOp",EDGE,"E80")}),-1.0]])]});
            var Q2;
            Q2=makeQuery(id+"F16.imprint","IMPRINT",FACE,{"disambiguationData":[TD([[makeQuery(id+"F16.imprint","IMPRINT",EDGE,{"derivedFrom":sQuery(id+"F16.wireOp",EDGE,"E87.MirrorCS")}),-1.0]])]});
            var Q3;
            Q3=makeQuery(id+"F2.opExtrude","CAP_FACE",FACE,{"disambiguationData":[OSD([sQuery(id+"F0.wireOp",EDGE,"E12"),sQuery(id+"F0.wireOp",EDGE,"E13"),sQuery(id+"F0.wireOp",EDGE,"E14"),sQuery(id+"F0.wireOp",EDGE,"E15"),sQuery(id+"F0.wireOp",EDGE,"E17.filletArc"),sQuery(id+"F0.wireOp",EDGE,"E18.filletArc"),sQuery(id+"F0.wireOp",EDGE,"E19.filletArc"),sQuery(id+"F0.wireOp",EDGE,"E20.filletArc"),sQuery(id+"F0.wireOp",EDGE,"E25.0"),sQuery(id+"F0.wireOp",EDGE,"E25.1"),sQuery(id+"F0.wireOp",EDGE,"E25.2"),sQuery(id+"F0.wireOp",EDGE,"E25.3"),sQuery(id+"F0.wireOp",EDGE,"E25.4"),sQuery(id+"F0.wireOp",EDGE,"E25.5"),sQuery(id+"F0.wireOp",EDGE,"E25.6"),sQuery(id+"F0.wireOp",EDGE,"E25.7")])],"isStart":false});
            extrude(context, id + "F17", {"entities" : qUnion([Q0, Q1, Q2]), "endBound" : BoundingType.UP_TO_SURFACE, "endBoundEntityFace" : qUnion([Q3]), "depth" : 25 * mm});
        }
    });
